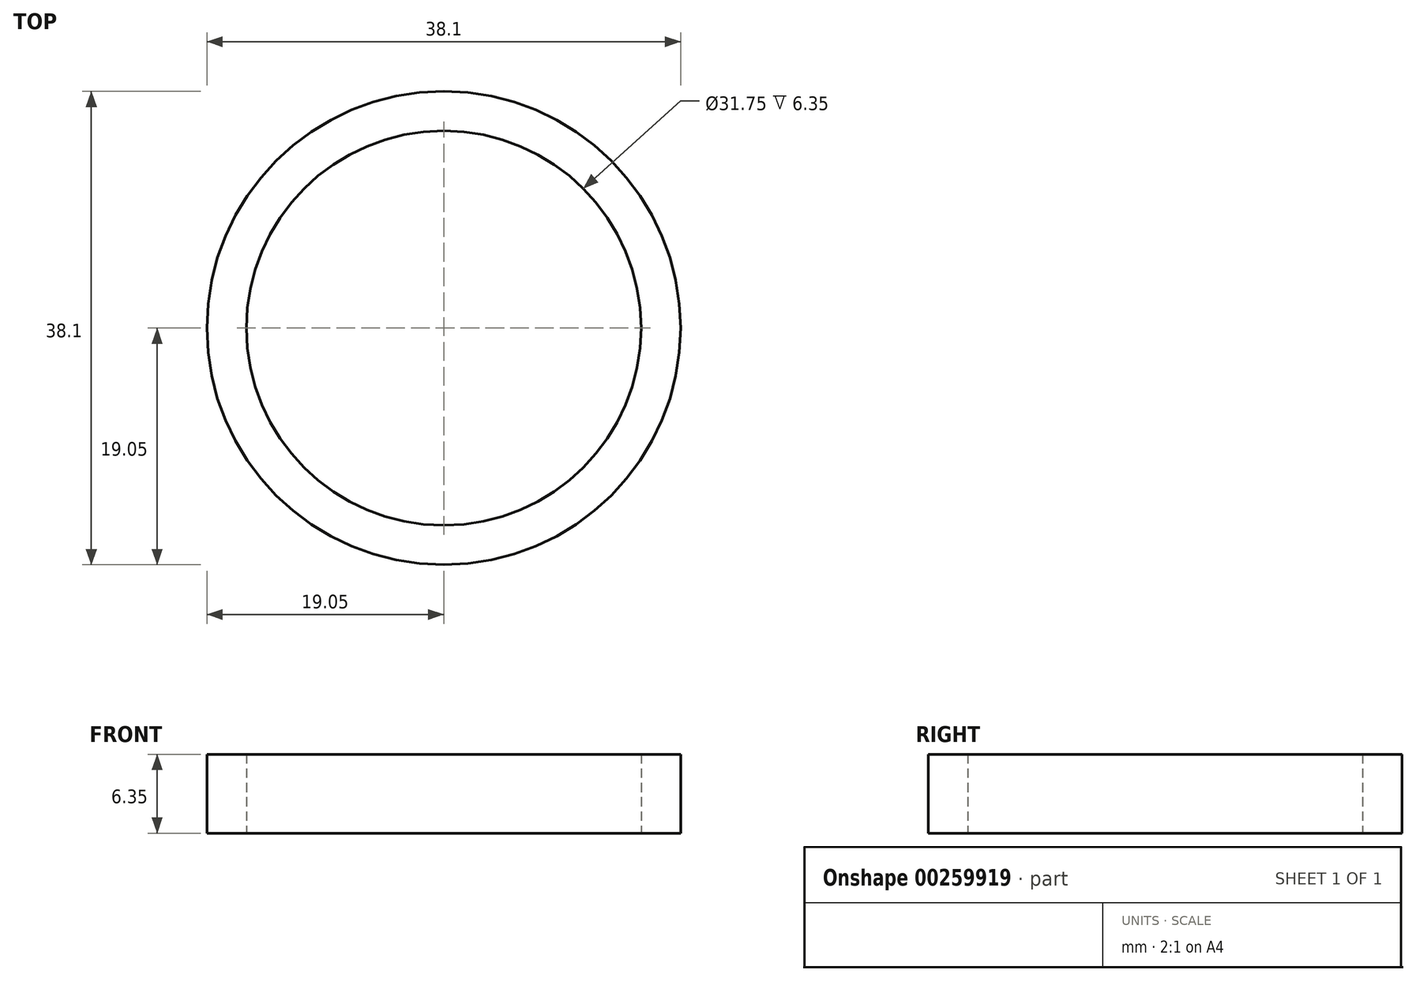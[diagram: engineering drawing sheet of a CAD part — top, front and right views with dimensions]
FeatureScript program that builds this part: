
annotation { "Feature Type Name" : "Feature", "Feature Type Description" : "" }
export const myFeature = defineFeature(function(context is Context, id is Id, definition is map)
    precondition{}
    {
        {
            var Q0;
            Q0=qCreatedBy(makeId("Top.planeOp"),FACE);
            var sketch = newSketch(context, id + "F0", { "sketchPlane" : qUnion([Q0])});
            skCircle(sketch, "E0", {"center": v(0, 0) * mm, "radius": 19.05 * mm});
            skCircle(sketch, "E1", {"center": v(0, 0) * mm, "radius": 15.88 * mm});
            skSolve(sketch);
        }
        {
            var Q0;
            Q0=makeQuery(id+"F0.imprint","IMPRINT",FACE,{"disambiguationData":[TD([[makeQuery(id+"F0.imprint","IMPRINT",EDGE,{"derivedFrom":sQuery(id+"F0.wireOp",EDGE,"E0")}),1.0]])]});
            extrude(context, id + "F1", {"entities" : qUnion([Q0]), "depth" : 6.35 * mm});
        }
    });
